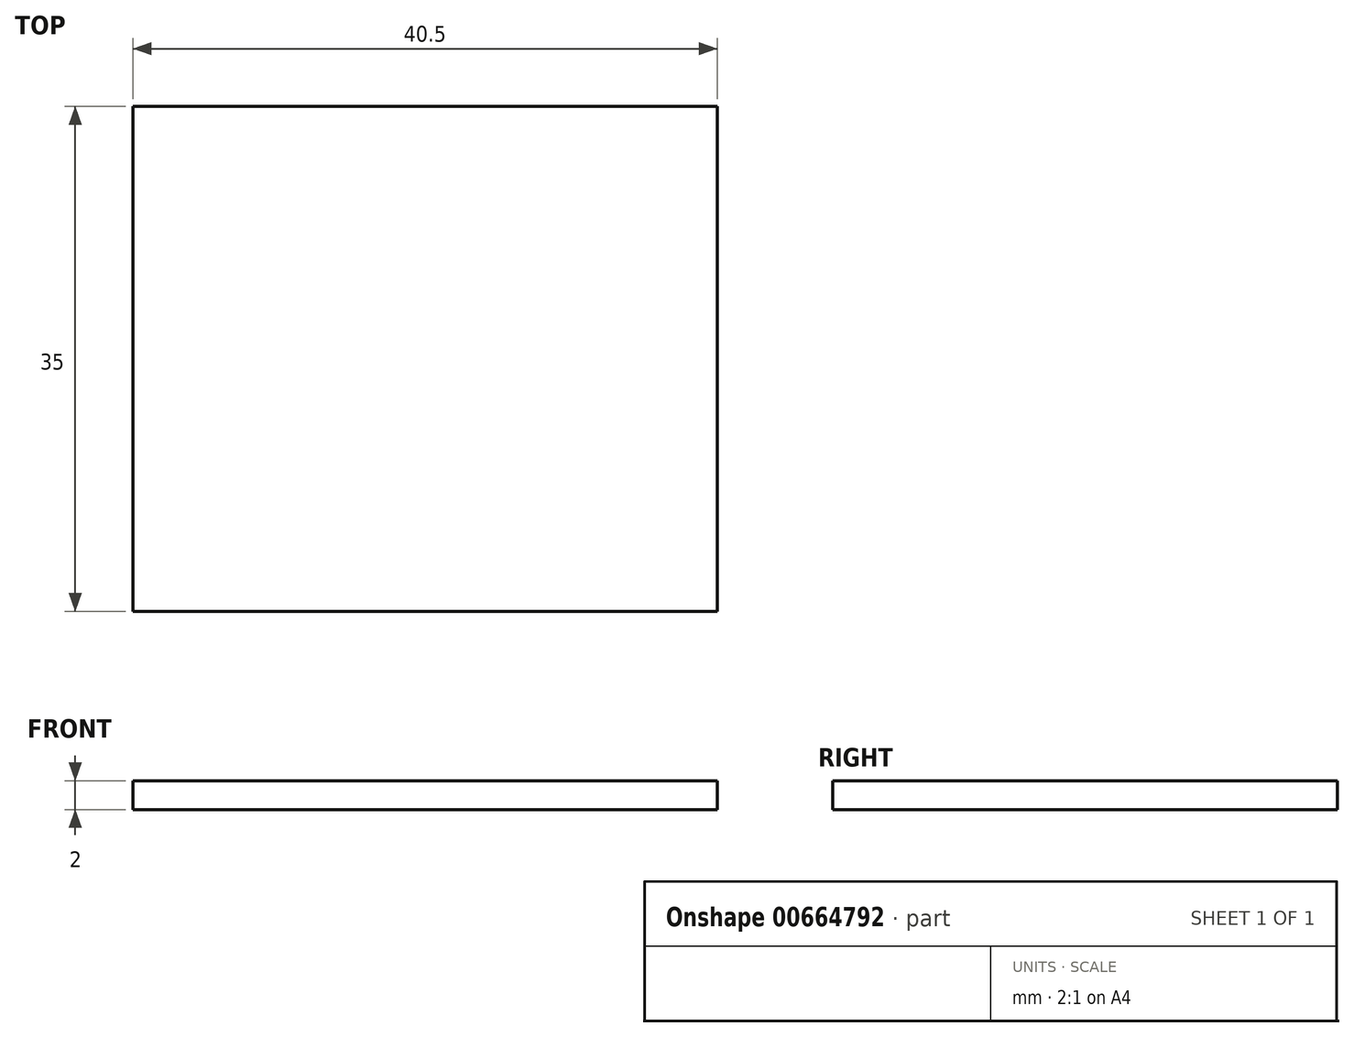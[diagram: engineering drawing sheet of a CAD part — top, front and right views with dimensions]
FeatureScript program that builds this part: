
annotation { "Feature Type Name" : "Feature", "Feature Type Description" : "" }
export const myFeature = defineFeature(function(context is Context, id is Id, definition is map)
    precondition{}
    {
        {
            var Q0;
            Q0=qCreatedBy(makeId("Top.planeOp"),FACE);
            var sketch = newSketch(context, id + "F0", { "sketchPlane" : qUnion([Q0])});
            skLineSegment(sketch, "E0.bottom", {"start": v(20.25, 17.5) * mm, "end": v(-20.25, 17.5) * mm});
            skLineSegment(sketch, "E0.top", {"start": v(20.25, -17.5) * mm, "end": v(-20.25, -17.5) * mm});
            skLineSegment(sketch, "E0.left", {"start": v(20.25, 17.5) * mm, "end": v(20.25, -17.5) * mm});
            skLineSegment(sketch, "E0.right", {"start": v(-20.25, 17.5) * mm, "end": v(-20.25, -17.5) * mm});
            skPoint(sketch, "E0.middle", {"position": v(0, 0) * mm});
            skSolve(sketch);
        }
        {
            var Q0;
            Q0 = qSketchRegion(id + "F0", true);
            extrude(context, id + "F1", {"entities" : qUnion([Q0]), "depth" : 2 * mm, "offsetDistance" : 25 * mm});
        }
    });
